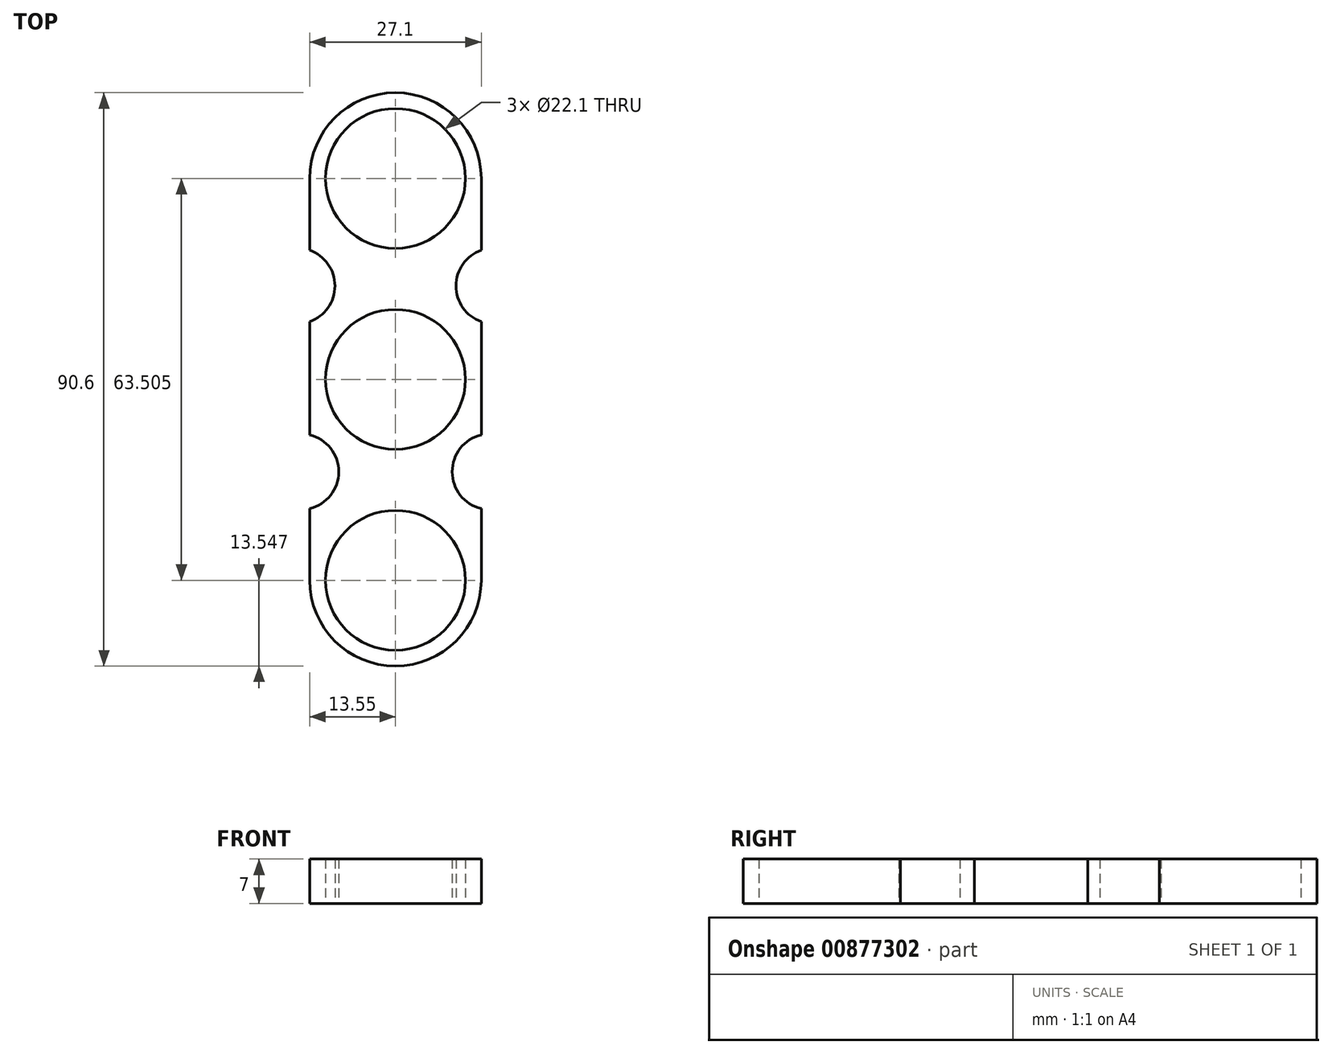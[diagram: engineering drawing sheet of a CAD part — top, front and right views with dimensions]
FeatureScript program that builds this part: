
annotation { "Feature Type Name" : "Feature", "Feature Type Description" : "" }
export const myFeature = defineFeature(function(context is Context, id is Id, definition is map)
    precondition{}
    {
        {
            var Q0;
            Q0=qCreatedBy(makeId("Top.planeOp"),FACE);
            var sketch = newSketch(context, id + "F0", { "sketchPlane" : qUnion([Q0])});
            skCircle(sketch, "E0", {"center": v(0, 0) * mm, "radius": 11.05 * mm});
            skCircle(sketch, "E1", {"center": v(0, 31.75) * mm, "radius": 11.05 * mm});
            skArc(sketch, "E2", {"start": v(13.55, 31.75) * mm, "mid": v(0, 45.3) * mm, "end": v(-13.55, 31.75) * mm});
            skArc(sketch, "E3.1.0", {"start": v(-13.55, -31.75) * mm, "mid": v(0, -45.3) * mm, "end": v(13.55, -31.75) * mm});
            skCircle(sketch, "E3.1.1", {"center": v(0, -31.75) * mm, "radius": 11.05 * mm});
            skLineSegment(sketch, "E4", {"start": v(13.55, -31.75) * mm, "end": v(13.55, -20.43) * mm});
            skLineSegment(sketch, "E5", {"start": v(-13.55, 31.75) * mm, "end": v(-13.55, 20.42) * mm});
            skArc(sketch, "E6", {"start": v(-13.55, -20.43) * mm, "mid": v(-8.95, -14.6) * mm, "end": v(-13.55, -8.77) * mm});
            skArc(sketch, "E7", {"start": v(-13.55, 9.12) * mm, "mid": v(-9.56, 14.77) * mm, "end": v(-13.55, 20.42) * mm});
            skArc(sketch, "E8", {"start": v(13.55, 20.42) * mm, "mid": v(9.56, 14.77) * mm, "end": v(13.55, 9.12) * mm});
            skArc(sketch, "E9", {"start": v(13.55, -8.77) * mm, "mid": v(8.95, -14.6) * mm, "end": v(13.55, -20.43) * mm});
            skLineSegment(sketch, "E10.trimOffspring", {"start": v(13.55, -8.77) * mm, "end": v(13.55, 9.12) * mm});
            skLineSegment(sketch, "E11.trimOffspring", {"start": v(13.55, 20.42) * mm, "end": v(13.55, 31.75) * mm});
            skLineSegment(sketch, "E12.trimOffspring", {"start": v(-13.55, 9.12) * mm, "end": v(-13.55, -8.77) * mm});
            skLineSegment(sketch, "E13.trimOffspring", {"start": v(-13.55, -20.43) * mm, "end": v(-13.55, -31.75) * mm});
            skSolve(sketch);
        }
        {
            var Q0;
            Q0 = qSketchRegion(id + "F0", true);
            extrude(context, id + "F1", {"entities" : qUnion([Q0]), "depth" : 7 * mm, "offsetDistance" : 25 * mm});
        }
    });
